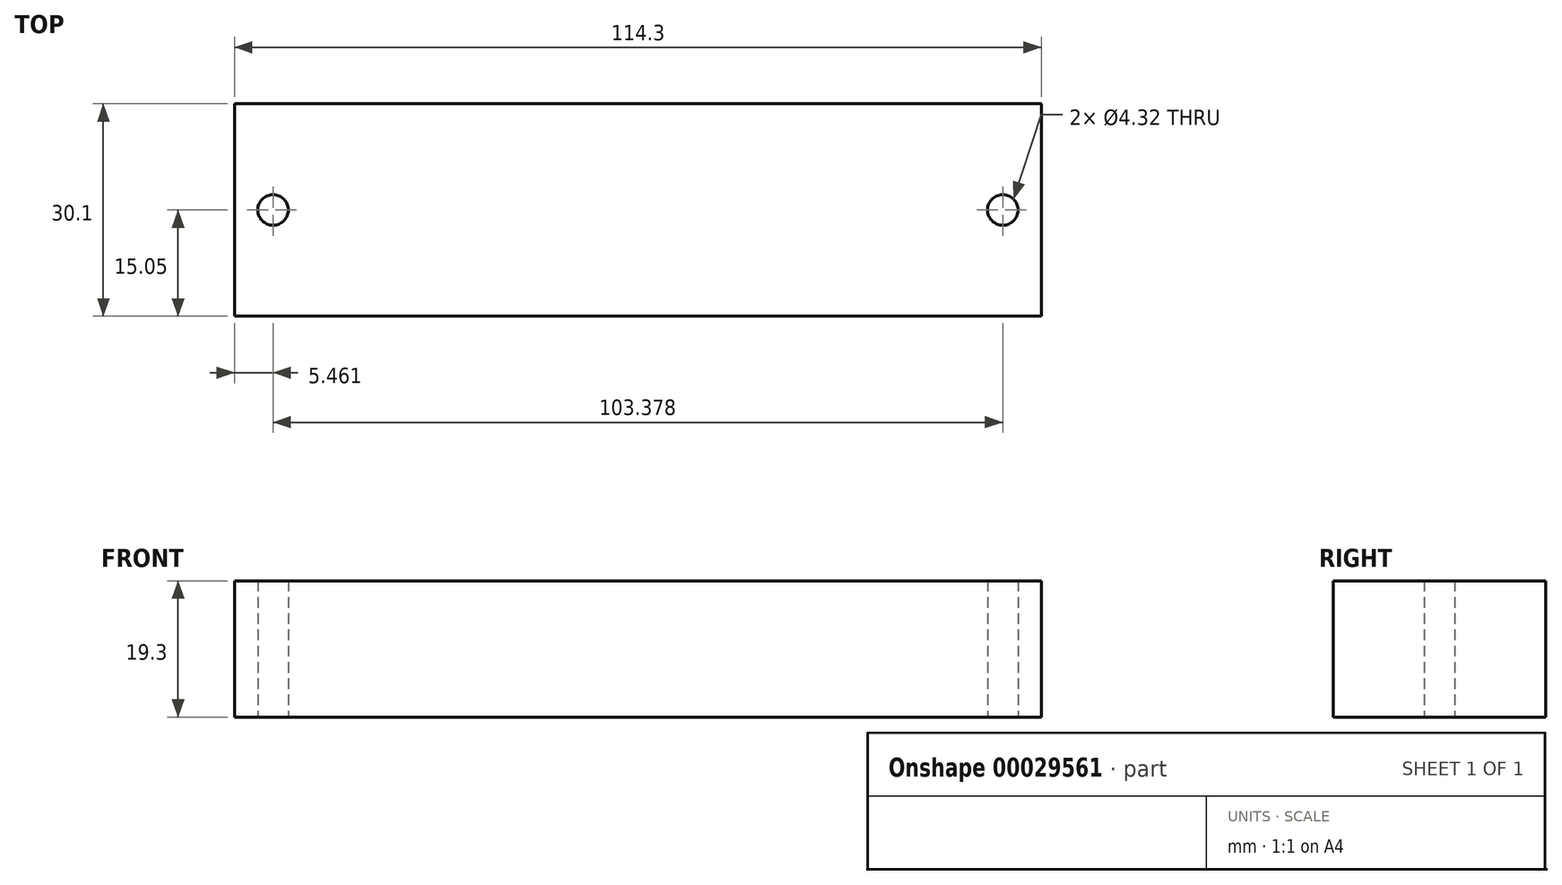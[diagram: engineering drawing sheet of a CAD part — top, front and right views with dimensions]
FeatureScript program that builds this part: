
annotation { "Feature Type Name" : "Feature", "Feature Type Description" : "" }
export const myFeature = defineFeature(function(context is Context, id is Id, definition is map)
    precondition{}
    {
        {
            var Q0;
            Q0=qCreatedBy(makeId("Top.planeOp"),FACE);
            var sketch = newSketch(context, id + "F0", { "sketchPlane" : qUnion([Q0])});
            skLineSegment(sketch, "E0.rect.bottom", {"start": v(57.15, 15.05) * mm, "end": v(-57.15, 15.05) * mm});
            skLineSegment(sketch, "E0.rect.top", {"start": v(57.15, -15.05) * mm, "end": v(-57.15, -15.05) * mm});
            skLineSegment(sketch, "E0.rect.left", {"start": v(57.15, 15.05) * mm, "end": v(57.15, -15.05) * mm});
            skLineSegment(sketch, "E0.rect.right", {"start": v(-57.15, 15.05) * mm, "end": v(-57.15, -15.05) * mm});
            skPoint(sketch, "E0.rect.middle", {"position": v(0, 0) * mm});
            skCircle(sketch, "E1", {"center": v(-51.69, 0) * mm, "radius": 2.16 * mm});
            skCircle(sketch, "E2", {"center": v(51.69, 0) * mm, "radius": 2.16 * mm});
            skSolve(sketch);
        }
        {
            var Q0;
            Q0 = qSketchRegion(id + "F0", true);
            extrude(context, id + "F1", {"entities" : qUnion([Q0]), "depth" : 19.3 * mm});
        }
    });
